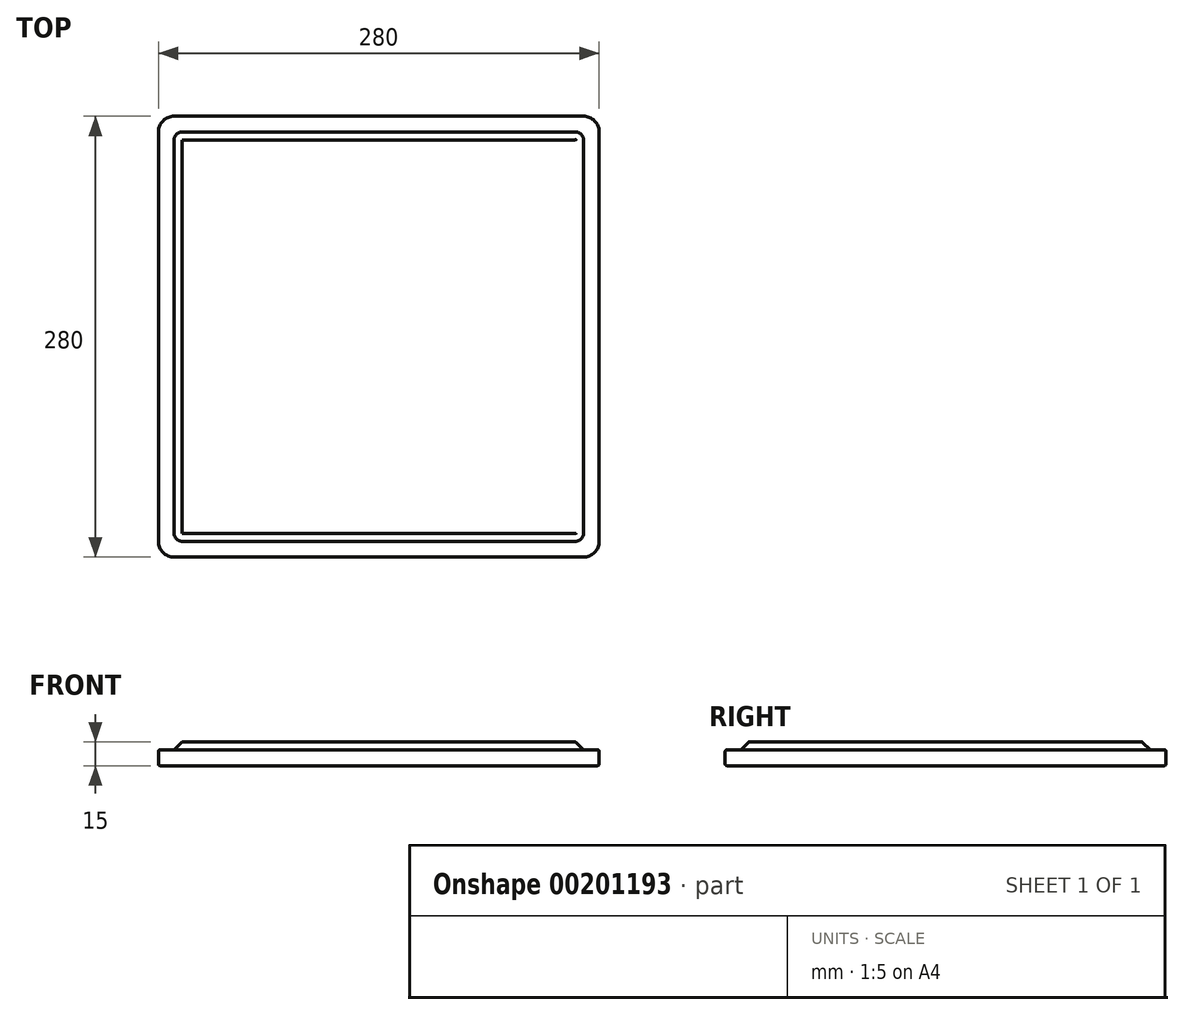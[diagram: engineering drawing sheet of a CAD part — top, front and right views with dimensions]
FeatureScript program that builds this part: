
annotation { "Feature Type Name" : "Feature", "Feature Type Description" : "" }
export const myFeature = defineFeature(function(context is Context, id is Id, definition is map)
    precondition{}
    {
        {
            var Q0;
            Q0=qCreatedBy(makeId("Top.planeOp"),FACE);
            var sketch = newSketch(context, id + "F0", { "sketchPlane" : qUnion([Q0])});
            skLineSegment(sketch, "E0.bottom", {"start": v(-130, 140) * mm, "end": v(130, 140) * mm});
            skLineSegment(sketch, "E0.top", {"start": v(-130, -140) * mm, "end": v(130, -140) * mm});
            skLineSegment(sketch, "E0.left", {"start": v(-140, 130) * mm, "end": v(-140, -130) * mm});
            skLineSegment(sketch, "E0.right", {"start": v(140, 130) * mm, "end": v(140, -130) * mm});
            skPoint(sketch, "E0.middle", {"position": v(0, 0) * mm});
            skPoint(sketch, "E1.visualSharp", {"position": v(-140, -140) * mm});
            skArc(sketch, "E1.filletArc", {"start": v(-140, -130) * mm, "mid": v(-137.07, -137.07) * mm, "end": v(-130, -140) * mm});
            skPoint(sketch, "E2.visualSharp", {"position": v(140, -140) * mm});
            skArc(sketch, "E2.filletArc", {"start": v(130, -140) * mm, "mid": v(137.07, -137.07) * mm, "end": v(140, -130) * mm});
            skPoint(sketch, "E3.visualSharp", {"position": v(140, 140) * mm});
            skArc(sketch, "E3.filletArc", {"start": v(140, 130) * mm, "mid": v(137.07, 137.07) * mm, "end": v(130, 140) * mm});
            skPoint(sketch, "E4.visualSharp", {"position": v(-140, 140) * mm});
            skArc(sketch, "E4.filletArc", {"start": v(-130, 140) * mm, "mid": v(-137.07, 137.07) * mm, "end": v(-140, 130) * mm});
            skSolve(sketch);
        }
        {
            var Q0;
            Q0=makeQuery(id+"F0.imprint","IMPRINT",FACE,{"disambiguationData":[TD([[makeQuery(id+"F0.imprint","IMPRINT",EDGE,{"derivedFrom":sQuery(id+"F0.wireOp",EDGE,"E0.bottom")}),-1.0]])]});
            extrude(context, id + "F1", {"entities" : qUnion([Q0]), "depth" : 10 * mm});
        }
        {
            var Q0;
            Q0=makeQuery(id+"F1.opExtrude","CAP_FACE",FACE,{"disambiguationData":[OSD([sQuery(id+"F0.wireOp",EDGE,"E0.bottom"),sQuery(id+"F0.wireOp",EDGE,"E0.top"),sQuery(id+"F0.wireOp",EDGE,"E0.left"),sQuery(id+"F0.wireOp",EDGE,"E0.right"),sQuery(id+"F0.wireOp",EDGE,"E1.filletArc"),sQuery(id+"F0.wireOp",EDGE,"E2.filletArc"),sQuery(id+"F0.wireOp",EDGE,"E3.filletArc"),sQuery(id+"F0.wireOp",EDGE,"E4.filletArc")])],"isStart":false});
            var sketch = newSketch(context, id + "F2", { "sketchPlane" : qUnion([Q0])});
            skLineSegment(sketch, "E5.bottom", {"start": v(-125, 130) * mm, "end": v(125, 130) * mm});
            skLineSegment(sketch, "E5.top", {"start": v(-125, -130) * mm, "end": v(125, -130) * mm});
            skLineSegment(sketch, "E5.left", {"start": v(-130, 125) * mm, "end": v(-130, -125) * mm});
            skLineSegment(sketch, "E5.right", {"start": v(130, 125) * mm, "end": v(130, -125) * mm});
            skPoint(sketch, "E5.middle", {"position": v(0, 0) * mm});
            skPoint(sketch, "E6.visualSharp", {"position": v(-130, 130) * mm});
            skArc(sketch, "E6.filletArc", {"start": v(-125, 130) * mm, "mid": v(-128.54, 128.54) * mm, "end": v(-130, 125) * mm});
            skPoint(sketch, "E7.visualSharp", {"position": v(130, 130) * mm});
            skArc(sketch, "E7.filletArc", {"start": v(130, 125) * mm, "mid": v(128.54, 128.54) * mm, "end": v(125, 130) * mm});
            skPoint(sketch, "E8.visualSharp", {"position": v(130, -130) * mm});
            skArc(sketch, "E8.filletArc", {"start": v(125, -130) * mm, "mid": v(128.54, -128.54) * mm, "end": v(130, -125) * mm});
            skPoint(sketch, "E9.visualSharp", {"position": v(-130, -130) * mm});
            skArc(sketch, "E9.filletArc", {"start": v(-130, -125) * mm, "mid": v(-128.54, -128.54) * mm, "end": v(-125, -130) * mm});
            skSolve(sketch);
        }
        {
            var Q0;
            Q0 = qSketchRegion(id + "F2", true);
            extrude(context, id + "F3", {"entities" : qUnion([Q0]), "operationType" : NewBodyOperationType.ADD, "depth" : 5 * mm, "hasDraft" : true, "draftAngle" : 45 * degree, "draftPullDirection" : true});
        }
        {
            var Q0;
            Q0=makeQuery(id+"F3.opExtrude","CAP_FACE",FACE,{"disambiguationData":[OSD([sQuery(id+"F2.wireOp",EDGE,"E5.bottom"),sQuery(id+"F2.wireOp",EDGE,"E5.top"),sQuery(id+"F2.wireOp",EDGE,"E5.left"),sQuery(id+"F2.wireOp",EDGE,"E5.right"),sQuery(id+"F2.wireOp",EDGE,"E6.filletArc"),sQuery(id+"F2.wireOp",EDGE,"E7.filletArc"),sQuery(id+"F2.wireOp",EDGE,"E8.filletArc"),sQuery(id+"F2.wireOp",EDGE,"E9.filletArc")])],"isStart":false});
            var sketch = newSketch(context, id + "F4", { "sketchPlane" : qUnion([Q0])});
            skCircle(sketch, "E10", {"center": v(0, 0) * mm, "radius": 65 * mm});
            skSolve(sketch);
        }
        {
            var Q0;
            Q0=makeQuery(id+"F4.imprint","IMPRINT",FACE,{"disambiguationData":[TD([[makeQuery(id+"F4.imprint","IMPRINT",EDGE,{"derivedFrom":makeQuery(id+"F3.opExtrude","CAP_EDGE",EDGE,{"disambiguationData":[OSD([sQuery(id+"F2.wireOp",EDGE,"E5.bottom")])],"isStart":false})}),-1.0]])]});
            var sketch = newSketch(context, id + "F5", { "sketchPlane" : qUnion([Q0])});
            skEllipse(sketch, "E11", {"center": v(0, 0) * mm, "majorRadius": 25 * mm, "minorRadius": 15 * mm, "majorAxis": v(0, 1)});
            skSolve(sketch);
        }
        {
            var Q0;
            Q0=makeQuery(id+"F5.imprint","IMPRINT",FACE,{"disambiguationData":[TD([[makeQuery(id+"F5.imprint","IMPRINT",EDGE,{"derivedFrom":makeQuery(id+"F4.imprint","IMPRINT",EDGE,{"derivedFrom":makeQuery(id+"F3.opExtrude","CAP_EDGE",EDGE,{"disambiguationData":[OSD([sQuery(id+"F2.wireOp",EDGE,"E5.bottom")])],"isStart":false})})}),-1.0]])]});
            var sketch = newSketch(context, id + "F6", { "sketchPlane" : qUnion([Q0])});
            skLineSegment(sketch, "E12.bottom", {"start": v(-40, 40) * mm, "end": v(40, 40) * mm});
            skLineSegment(sketch, "E12.top", {"start": v(-40, -40) * mm, "end": v(40, -40) * mm});
            skLineSegment(sketch, "E12.left", {"start": v(-40, 40) * mm, "end": v(-40, -40) * mm});
            skLineSegment(sketch, "E12.right", {"start": v(40, 40) * mm, "end": v(40, -40) * mm});
            skPoint(sketch, "E12.middle", {"position": v(0, 0) * mm});
            skSolve(sketch);
        }
        {
            var Q0;
            Q0=makeQuery(id+"F3.opExtrude","CAP_FACE",FACE,{"disambiguationData":[OSD([sQuery(id+"F2.wireOp",EDGE,"E5.bottom"),sQuery(id+"F2.wireOp",EDGE,"E5.top"),sQuery(id+"F2.wireOp",EDGE,"E5.left"),sQuery(id+"F2.wireOp",EDGE,"E5.right"),sQuery(id+"F2.wireOp",EDGE,"E6.filletArc"),sQuery(id+"F2.wireOp",EDGE,"E7.filletArc"),sQuery(id+"F2.wireOp",EDGE,"E8.filletArc"),sQuery(id+"F2.wireOp",EDGE,"E9.filletArc")])],"isStart":false});
            var sketch = newSketch(context, id + "F7", { "sketchPlane" : qUnion([Q0])});
            skLineSegment(sketch, "E13.bottom", {"start": v(-45, 55) * mm, "end": v(45, 55) * mm});
            skLineSegment(sketch, "E13.top", {"start": v(-45, -55) * mm, "end": v(45, -55) * mm});
            skLineSegment(sketch, "E13.left", {"start": v(-45, 55) * mm, "end": v(-45, -55) * mm});
            skLineSegment(sketch, "E13.right", {"start": v(45, 55) * mm, "end": v(45, -55) * mm});
            skPoint(sketch, "E13.middle", {"position": v(0, 0) * mm});
            skSolve(sketch);
        }
        {
            var Q0;
            Q0=makeQuery(id+"F1.opExtrude","CAP_EDGE",EDGE,{"disambiguationData":[OSD([sQuery(id+"F0.wireOp",EDGE,"E0.right")])],"isStart":false});
            var Q1;
            Q1=makeQuery(id+"F1.opExtrude","CAP_EDGE",EDGE,{"disambiguationData":[OSD([sQuery(id+"F0.wireOp",EDGE,"E0.right")])],"isStart":true});
            var Q2;
            Q2=makeQuery(id+"F3.opExtrude","CAP_EDGE",EDGE,{"disambiguationData":[OSD([sQuery(id+"F2.wireOp",EDGE,"E5.right")])],"isStart":true});
            var Q3;
            Q3=makeQuery(id+"F3.opExtrude","CAP_EDGE",EDGE,{"disambiguationData":[OSD([sQuery(id+"F2.wireOp",EDGE,"E5.right")])],"isStart":false});
            fillet(context, id + "F8", {"entities" : qUnion([Q0, Q1, Q2, Q3]), "radius" : 1 * mm, "tangentPropagation" : true, "allowEdgeOverflow" : false});
        }
    });
